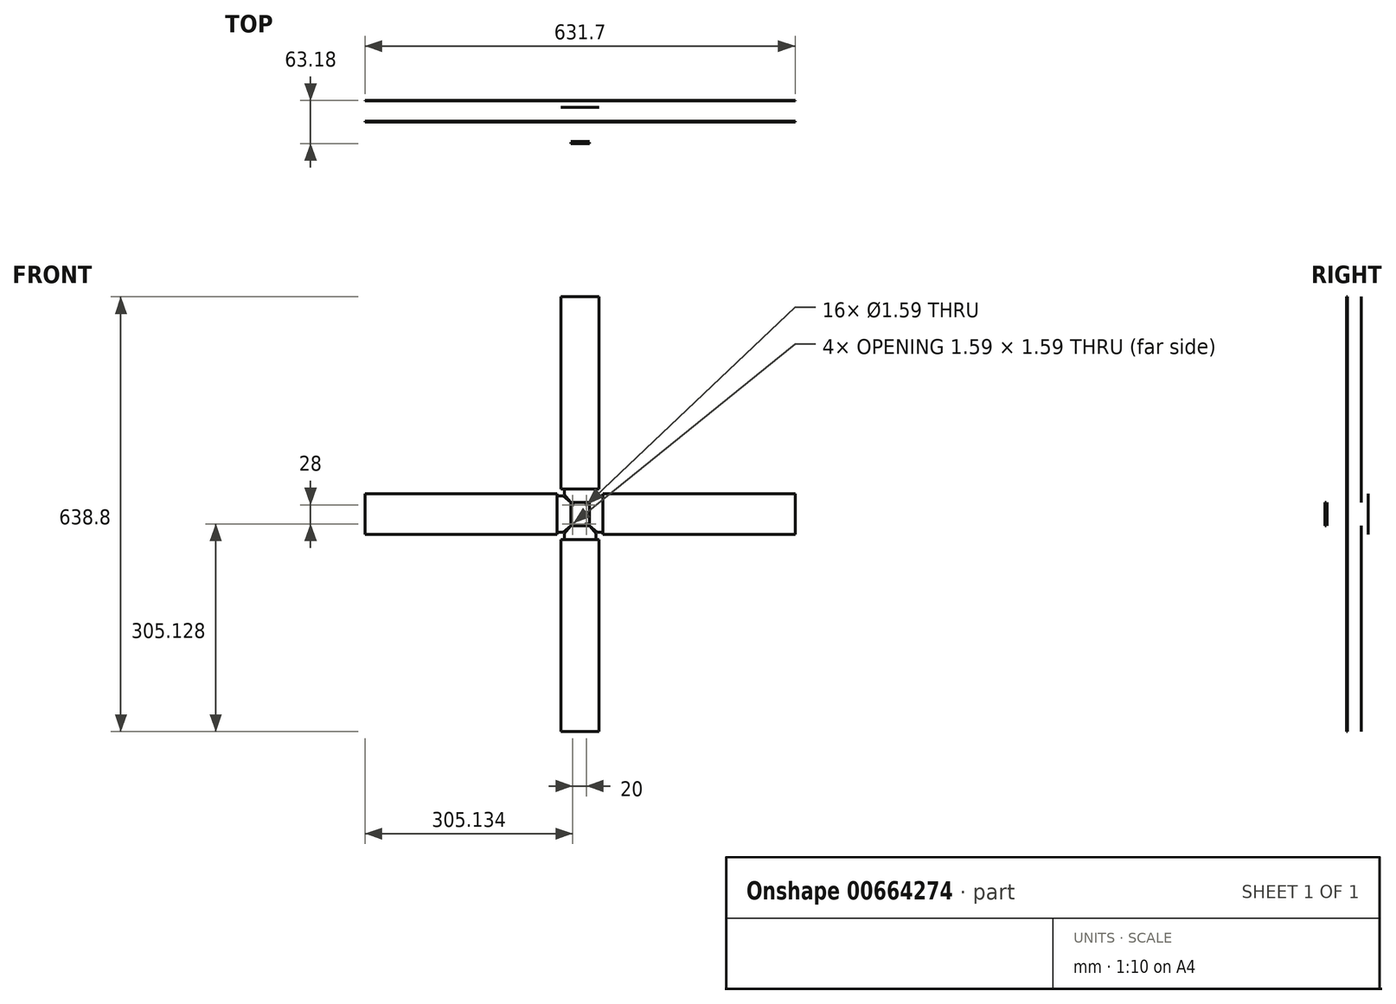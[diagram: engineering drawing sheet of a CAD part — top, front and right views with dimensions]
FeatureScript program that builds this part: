
annotation { "Feature Type Name" : "Feature", "Feature Type Description" : "" }
export const myFeature = defineFeature(function(context is Context, id is Id, definition is map)
    precondition{}
    {
        {
            var Q0;
            Q0=qCreatedBy(makeId("Front.planeOp"),FACE);
            var sketch = newSketch(context, id + "F0", { "sketchPlane" : qUnion([Q0])});
            skLineSegment(sketch, "E0.bottom", {"start": v(13.72, -17.27) * mm, "end": v(-13.72, -17.27) * mm});
            skLineSegment(sketch, "E0.top", {"start": v(13.72, 17.27) * mm, "end": v(-13.72, 17.27) * mm});
            skLineSegment(sketch, "E0.left", {"start": v(13.72, -17.27) * mm, "end": v(13.72, 17.27) * mm});
            skLineSegment(sketch, "E0.right", {"start": v(-13.72, -17.27) * mm, "end": v(-13.72, 17.27) * mm});
            skPoint(sketch, "E0.middle", {"position": v(0, 0) * mm});
            skLineSegment(sketch, "E1", {"start": v(0, 0) * mm, "end": v(200.92, 0) * mm, "construction": true});
            skLineSegment(sketch, "E2.bottom", {"start": v(33.66, -29.97) * mm, "end": v(315.85, -29.97) * mm});
            skLineSegment(sketch, "E2.top", {"start": v(33.66, 29.97) * mm, "end": v(315.85, 29.97) * mm});
            skLineSegment(sketch, "E2.left", {"start": v(33.66, -29.97) * mm, "end": v(33.66, 29.97) * mm});
            skLineSegment(sketch, "E2.right", {"start": v(315.85, -29.97) * mm, "end": v(315.85, 29.97) * mm});
            skLineSegment(sketch, "E3", {"start": v(33.66, 26.8) * mm, "end": v(25.07, 26.8) * mm});
            skLineSegment(sketch, "E4", {"start": v(25.07, 26.8) * mm, "end": v(13.72, 17.27) * mm});
            skLineSegment(sketch, "E5", {"start": v(33.66, -26.8) * mm, "end": v(25.07, -26.8) * mm});
            skLineSegment(sketch, "E6", {"start": v(25.07, -26.8) * mm, "end": v(13.72, -17.27) * mm});
            skLineSegment(sketch, "E7", {"start": v(0, 0) * mm, "end": v(0, 94.18) * mm, "construction": true});
            skLineSegment(sketch, "E8.bottom", {"start": v(-27.94, 37.21) * mm, "end": v(27.94, 37.21) * mm});
            skLineSegment(sketch, "E8.top", {"start": v(-27.94, 319.4) * mm, "end": v(27.94, 319.4) * mm});
            skLineSegment(sketch, "E8.left", {"start": v(-27.94, 37.21) * mm, "end": v(-27.94, 319.4) * mm});
            skLineSegment(sketch, "E8.right", {"start": v(27.94, 37.21) * mm, "end": v(27.94, 319.4) * mm});
            skLineSegment(sketch, "E9", {"start": v(-23.24, 37.21) * mm, "end": v(-23.24, 28.62) * mm});
            skLineSegment(sketch, "E10", {"start": v(-23.24, 28.62) * mm, "end": v(-13.72, 17.27) * mm});
            skLineSegment(sketch, "E11", {"start": v(23.24, 37.21) * mm, "end": v(23.24, 28.62) * mm});
            skLineSegment(sketch, "E12", {"start": v(23.24, 28.62) * mm, "end": v(13.72, 17.27) * mm});
            skSolve(sketch);
        }
        {
            var Q0;
            Q0=makeQuery(id+"F0.imprint","IMPRINT",FACE,{"disambiguationData":[TD([[makeQuery(id+"F0.imprint","IMPRINT",EDGE,{"derivedFrom":sQuery(id+"F0.wireOp",EDGE,"E0.bottom")}),-1.0]])]});
            extrude(context, id + "F1", {"entities" : qUnion([Q0]), "depth" : 0.2 * mm, "offsetDistance" : 25.4 * mm});
        }
        {
            var Q0;
            Q0=makeQuery(id+"F1.opExtrude","CAP_FACE",FACE,{"disambiguationData":[OSD([sQuery(id+"F0.wireOp",EDGE,"E0.bottom"),sQuery(id+"F0.wireOp",EDGE,"E0.top"),sQuery(id+"F0.wireOp",EDGE,"E0.right"),sQuery(id+"F0.wireOp",EDGE,"E2.bottom"),sQuery(id+"F0.wireOp",EDGE,"E2.top"),sQuery(id+"F0.wireOp",EDGE,"E2.left"),sQuery(id+"F0.wireOp",EDGE,"E2.right"),sQuery(id+"F0.wireOp",EDGE,"E3"),sQuery(id+"F0.wireOp",EDGE,"E4"),sQuery(id+"F0.wireOp",EDGE,"E5"),sQuery(id+"F0.wireOp",EDGE,"E6")])],"isStart":false});
            extrude(context, id + "F2", {"entities" : qUnion([Q0]), "depth" : (0.06 * 25.4 - 0.2) * mm, "offsetDistance" : 25 * mm});
        }
        {
            var Q0;
            Q0=makeQuery(id+"F0.imprint","IMPRINT",FACE,{"disambiguationData":[TD([[makeQuery(id+"F0.imprint","IMPRINT",EDGE,{"derivedFrom":sQuery(id+"F0.wireOp",EDGE,"E0.bottom")}),-1.0]])]});
            extrude(context, id + "F3", {"entities" : qUnion([Q0]), "depth" : (0.12 * 25.4) * mm, "offsetDistance" : 25 * mm});
        }
        {
            var Q0;
            Q0=makeQuery(id+"F2.opExtrude","SWEPT_BODY",BODY,{"disambiguationData":[OSD([sQuery(id+"F0.wireOp",EDGE,"E0.bottom"),sQuery(id+"F0.wireOp",EDGE,"E0.top"),sQuery(id+"F0.wireOp",EDGE,"E0.right"),sQuery(id+"F0.wireOp",EDGE,"E2.bottom"),sQuery(id+"F0.wireOp",EDGE,"E2.top"),sQuery(id+"F0.wireOp",EDGE,"E2.left"),sQuery(id+"F0.wireOp",EDGE,"E2.right"),sQuery(id+"F0.wireOp",EDGE,"E3"),sQuery(id+"F0.wireOp",EDGE,"E4"),sQuery(id+"F0.wireOp",EDGE,"E5"),sQuery(id+"F0.wireOp",EDGE,"E6")])]});
            var Q1;
            Q1=makeQuery(id+"F3.opExtrude","SWEPT_BODY",BODY,{"disambiguationData":[OSD([sQuery(id+"F0.wireOp",EDGE,"E0.bottom"),sQuery(id+"F0.wireOp",EDGE,"E0.top"),sQuery(id+"F0.wireOp",EDGE,"E0.left"),sQuery(id+"F0.wireOp",EDGE,"E0.right")])]});
            booleanBodies(context, id + "F4", {"operationType" : BooleanOperationType.SUBTRACTION, "tools" : qUnion([Q0]), "targets" : qUnion([Q1]), "keepTools" : true});
        }
        {
            var Q0;
            Q0=makeQuery(id+"F1.opExtrude","CAP_FACE",FACE,{"disambiguationData":[OSD([sQuery(id+"F0.wireOp",EDGE,"E0.bottom"),sQuery(id+"F0.wireOp",EDGE,"E0.top"),sQuery(id+"F0.wireOp",EDGE,"E0.right"),sQuery(id+"F0.wireOp",EDGE,"E2.bottom"),sQuery(id+"F0.wireOp",EDGE,"E2.top"),sQuery(id+"F0.wireOp",EDGE,"E2.left"),sQuery(id+"F0.wireOp",EDGE,"E2.right"),sQuery(id+"F0.wireOp",EDGE,"E3"),sQuery(id+"F0.wireOp",EDGE,"E4"),sQuery(id+"F0.wireOp",EDGE,"E5"),sQuery(id+"F0.wireOp",EDGE,"E6")])],"isStart":true});
            var sketch = newSketch(context, id + "F5", { "sketchPlane" : qUnion([Q0])});
            skCircle(sketch, "E13", {"center": v(10.72, -14.27) * mm, "radius": 0.8 * mm});
            skCircle(sketch, "E14.0.1.0", {"center": v(10.72, 13.73) * mm, "radius": 0.8 * mm});
            skCircle(sketch, "E14.1.0.0", {"center": v(-9.28, -14.27) * mm, "radius": 0.8 * mm});
            skCircle(sketch, "E14.1.1.0", {"center": v(-9.28, 13.73) * mm, "radius": 0.8 * mm});
            skLineSegment(sketch, "E14.direction1", {"start": v(-9.28, -14.27) * mm, "end": v(10.72, -14.27) * mm, "construction": true});
            skLineSegment(sketch, "E14.direction2", {"start": v(10.72, -14.27) * mm, "end": v(10.72, 13.73) * mm, "construction": true});
            skSolve(sketch);
        }
        {
            var Q0;
            Q0 = qSketchRegion(id + "F5", true);
            extrude(context, id + "F6", {"entities" : qUnion([Q0]), "operationType" : NewBodyOperationType.REMOVE, "endBound" : BoundingType.THROUGH_ALL, "oppositeDirection" : true, "depth" : 25 * mm, "offsetDistance" : 25 * mm});
        }
        {
            var Q0;
            Q0=makeQuery(id+"F0.imprint","IMPRINT",FACE,{"disambiguationData":[TD([[makeQuery(id+"F0.imprint","IMPRINT",EDGE,{"derivedFrom":sQuery(id+"F0.wireOp",EDGE,"E0.top")}),-1.0]])]});
            var Q1;
            Q1=makeQuery(id+"F0.imprint","IMPRINT",FACE,{"disambiguationData":[TD([[makeQuery(id+"F0.imprint","IMPRINT",EDGE,{"derivedFrom":sQuery(id+"F0.wireOp",EDGE,"E0.left")}),-1.0]])]});
            extrude(context, id + "F7", {"entities" : qUnion([Q0, Q1]), "depth" : 0.2 * mm, "offsetDistance" : 25 * mm});
        }
        {
            var Q0;
            Q0=makeQuery(id+"F0.imprint","IMPRINT",FACE,{"disambiguationData":[TD([[makeQuery(id+"F0.imprint","IMPRINT",EDGE,{"derivedFrom":sQuery(id+"F0.wireOp",EDGE,"E8.top")}),-1.0]])]});
            var Q1;
            {var subQ3=sQuery(id+"F0.wireOp",EDGE,"E2.bottom");Q1=makeQuery(id+"F0.imprint","IMPRINT",FACE,{"disambiguationData":[TD([[makeQuery(id+"F0.imprint","IMPRINT",EDGE,{"derivedFrom":subQ3}),1.0]])]});}
            extrude(context, id + "F8", {"entities" : qUnion([Q0, Q1]), "depth" : 0.2 * mm, "offsetDistance" : 25 * mm});
        }
        {
            var Q0;
            Q0=makeQuery(id+"F8.opExtrude","CAP_FACE",FACE,{"disambiguationData":[OSD([sQuery(id+"F0.wireOp",EDGE,"E8.bottom"),sQuery(id+"F0.wireOp",EDGE,"E8.top"),sQuery(id+"F0.wireOp",EDGE,"E8.left"),sQuery(id+"F0.wireOp",EDGE,"E8.right")])],"isStart":false});
            var Q1;
            Q1=makeQuery(id+"F8.opExtrude","CAP_FACE",FACE,{"disambiguationData":[OSD([sQuery(id+"F0.wireOp",EDGE,"E2.bottom"),sQuery(id+"F0.wireOp",EDGE,"E2.top"),sQuery(id+"F0.wireOp",EDGE,"E2.left"),sQuery(id+"F0.wireOp",EDGE,"E2.right")])],"isStart":false});
            var Q2;
            Q2=makeQuery(id+"F7.opExtrude","CAP_FACE",FACE,{"disambiguationData":[OSD([sQuery(id+"F0.wireOp",EDGE,"E0.top"),sQuery(id+"F0.wireOp",EDGE,"E8.bottom"),sQuery(id+"F0.wireOp",EDGE,"E9"),sQuery(id+"F0.wireOp",EDGE,"E10"),sQuery(id+"F0.wireOp",EDGE,"E11"),sQuery(id+"F0.wireOp",EDGE,"E12")])],"isStart":false});
            var Q3;
            Q3=makeQuery(id+"F7.opExtrude","CAP_FACE",FACE,{"disambiguationData":[OSD([sQuery(id+"F0.wireOp",EDGE,"E0.left"),sQuery(id+"F0.wireOp",EDGE,"E2.left"),sQuery(id+"F0.wireOp",EDGE,"E3"),sQuery(id+"F0.wireOp",EDGE,"E4"),sQuery(id+"F0.wireOp",EDGE,"E5"),sQuery(id+"F0.wireOp",EDGE,"E6")])],"isStart":false});
            extrude(context, id + "F9", {"entities" : qUnion([Q0, Q1, Q2, Q3]), "depth" : 1.3 * mm, "offsetDistance" : 25 * mm});
        }
        {
            var Q0;
            Q0=makeQuery(id+"F4.opBoolean","SPLIT",BODY,{"disambiguationData":[OD(1.0)],"derivedFrom":makeQuery(id+"F3.opExtrude","SWEPT_BODY",BODY,{"disambiguationData":[OSD([sQuery(id+"F0.wireOp",EDGE,"E0.bottom"),sQuery(id+"F0.wireOp",EDGE,"E0.top"),sQuery(id+"F0.wireOp",EDGE,"E0.left"),sQuery(id+"F0.wireOp",EDGE,"E0.right")])]})});
            transform(context, id + "F10", {"entities" : qUnion([Q0]), "transformType" : TransformType.TRANSLATION_3D, "dx" : 0 * mm, "dy" : -10 * mm, "dz" : 0 * mm, "makeCopy" : false});
        }
        {
            var Q0;
            Q0=makeQuery(id+"F1.opExtrude","SWEPT_BODY",BODY,{"disambiguationData":[OSD([sQuery(id+"F0.wireOp",EDGE,"E0.bottom"),sQuery(id+"F0.wireOp",EDGE,"E0.top"),sQuery(id+"F0.wireOp",EDGE,"E0.left"),sQuery(id+"F0.wireOp",EDGE,"E0.right")])]});
            var Q1;
            Q1=makeQuery(id+"F7.opExtrude","SWEPT_BODY",BODY,{"disambiguationData":[OSD([sQuery(id+"F0.wireOp",EDGE,"E0.left"),sQuery(id+"F0.wireOp",EDGE,"E2.left"),sQuery(id+"F0.wireOp",EDGE,"E3"),sQuery(id+"F0.wireOp",EDGE,"E4"),sQuery(id+"F0.wireOp",EDGE,"E5"),sQuery(id+"F0.wireOp",EDGE,"E6")])]});
            var Q2;
            Q2=makeQuery(id+"F8.opExtrude","SWEPT_BODY",BODY,{"disambiguationData":[OSD([sQuery(id+"F0.wireOp",EDGE,"E2.bottom"),sQuery(id+"F0.wireOp",EDGE,"E2.top"),sQuery(id+"F0.wireOp",EDGE,"E2.left"),sQuery(id+"F0.wireOp",EDGE,"E2.right")])]});
            transform(context, id + "F11", {"entities" : qUnion([Q0, Q1, Q2]), "transformType" : TransformType.TRANSLATION_3D, "dx" : 0 * mm, "dy" : 10 * mm, "dz" : 0 * mm, "makeCopy" : false});
        }
        {
            var Q0;
            Q0=makeQuery(id+"F8.opExtrude","SWEPT_BODY",BODY,{"disambiguationData":[OSD([sQuery(id+"F0.wireOp",EDGE,"E8.bottom"),sQuery(id+"F0.wireOp",EDGE,"E8.top"),sQuery(id+"F0.wireOp",EDGE,"E8.left"),sQuery(id+"F0.wireOp",EDGE,"E8.right")])]});
            var Q1;
            Q1=makeQuery(id+"F7.opExtrude","SWEPT_BODY",BODY,{"disambiguationData":[OSD([sQuery(id+"F0.wireOp",EDGE,"E0.top"),sQuery(id+"F0.wireOp",EDGE,"E8.bottom"),sQuery(id+"F0.wireOp",EDGE,"E9"),sQuery(id+"F0.wireOp",EDGE,"E10"),sQuery(id+"F0.wireOp",EDGE,"E11"),sQuery(id+"F0.wireOp",EDGE,"E12")])]});
            var Q2;
            Q2=makeQuery(id+"F9.opExtrude","SWEPT_BODY",BODY,{"disambiguationData":[OSD([sQuery(id+"F0.wireOp",EDGE,"E8.bottom"),sQuery(id+"F0.wireOp",EDGE,"E8.top"),sQuery(id+"F0.wireOp",EDGE,"E8.left"),sQuery(id+"F0.wireOp",EDGE,"E8.right")])]});
            var Q3;
            Q3=makeQuery(id+"F9.opExtrude","SWEPT_BODY",BODY,{"disambiguationData":[OSD([sQuery(id+"F0.wireOp",EDGE,"E0.top"),sQuery(id+"F0.wireOp",EDGE,"E8.bottom"),sQuery(id+"F0.wireOp",EDGE,"E9"),sQuery(id+"F0.wireOp",EDGE,"E10"),sQuery(id+"F0.wireOp",EDGE,"E11"),sQuery(id+"F0.wireOp",EDGE,"E12")])]});
            var Q4;
            Q4=qCreatedBy(makeId("Top.planeOp"),FACE);
            mirror(context, id + "F12", {"entities" : qUnion([Q0, Q1, Q2, Q3]), "mirrorPlane" : qUnion([Q4])});
        }
        {
            var Q0;
            Q0=makeQuery(id+"F8.opExtrude","SWEPT_BODY",BODY,{"disambiguationData":[OSD([sQuery(id+"F0.wireOp",EDGE,"E2.bottom"),sQuery(id+"F0.wireOp",EDGE,"E2.top"),sQuery(id+"F0.wireOp",EDGE,"E2.left"),sQuery(id+"F0.wireOp",EDGE,"E2.right")])]});
            var Q1;
            Q1=makeQuery(id+"F7.opExtrude","SWEPT_BODY",BODY,{"disambiguationData":[OSD([sQuery(id+"F0.wireOp",EDGE,"E0.left"),sQuery(id+"F0.wireOp",EDGE,"E2.left"),sQuery(id+"F0.wireOp",EDGE,"E3"),sQuery(id+"F0.wireOp",EDGE,"E4"),sQuery(id+"F0.wireOp",EDGE,"E5"),sQuery(id+"F0.wireOp",EDGE,"E6")])]});
            var Q2;
            Q2=makeQuery(id+"F9.opExtrude","SWEPT_BODY",BODY,{"disambiguationData":[OSD([sQuery(id+"F0.wireOp",EDGE,"E2.bottom"),sQuery(id+"F0.wireOp",EDGE,"E2.top"),sQuery(id+"F0.wireOp",EDGE,"E2.left"),sQuery(id+"F0.wireOp",EDGE,"E2.right")])]});
            var Q3;
            Q3=makeQuery(id+"F9.opExtrude","SWEPT_BODY",BODY,{"disambiguationData":[OSD([sQuery(id+"F0.wireOp",EDGE,"E0.left"),sQuery(id+"F0.wireOp",EDGE,"E2.left"),sQuery(id+"F0.wireOp",EDGE,"E3"),sQuery(id+"F0.wireOp",EDGE,"E4"),sQuery(id+"F0.wireOp",EDGE,"E5"),sQuery(id+"F0.wireOp",EDGE,"E6")])]});
            var Q4;
            Q4=qCreatedBy(makeId("Right.planeOp"),FACE);
            mirror(context, id + "F13", {"entities" : qUnion([Q0, Q1, Q2, Q3]), "mirrorPlane" : qUnion([Q4])});
        }
        {
            var Q0;
            Q0=makeQuery(id+"F4.opBoolean","SPLIT",BODY,{"disambiguationData":[OD(1.0)],"derivedFrom":makeQuery(id+"F3.opExtrude","SWEPT_BODY",BODY,{"disambiguationData":[OSD([sQuery(id+"F0.wireOp",EDGE,"E0.bottom"),sQuery(id+"F0.wireOp",EDGE,"E0.top"),sQuery(id+"F0.wireOp",EDGE,"E0.left"),sQuery(id+"F0.wireOp",EDGE,"E0.right")])]})});
            transform(context, id + "F14", {"entities" : qUnion([Q0]), "transformType" : TransformType.TRANSLATION_3D, "dx" : 0 * mm, "dy" : -20 * mm, "dz" : 0 * mm, "makeCopy" : false});
        }
        {
            var Q0;
            Q0=makeQuery(id+"F1.opExtrude","SWEPT_BODY",BODY,{"disambiguationData":[OSD([sQuery(id+"F0.wireOp",EDGE,"E0.bottom"),sQuery(id+"F0.wireOp",EDGE,"E0.top"),sQuery(id+"F0.wireOp",EDGE,"E0.right"),sQuery(id+"F0.wireOp",EDGE,"E2.bottom"),sQuery(id+"F0.wireOp",EDGE,"E2.top"),sQuery(id+"F0.wireOp",EDGE,"E2.left"),sQuery(id+"F0.wireOp",EDGE,"E2.right"),sQuery(id+"F0.wireOp",EDGE,"E3"),sQuery(id+"F0.wireOp",EDGE,"E4"),sQuery(id+"F0.wireOp",EDGE,"E5"),sQuery(id+"F0.wireOp",EDGE,"E6")])]});
            var Q1;
            Q1=makeQuery(id+"F13.opPattern","COPY",BODY,{"derivedFrom":makeQuery(id+"F7.opExtrude","SWEPT_BODY",BODY,{"disambiguationData":[OSD([sQuery(id+"F0.wireOp",EDGE,"E0.left"),sQuery(id+"F0.wireOp",EDGE,"E2.left"),sQuery(id+"F0.wireOp",EDGE,"E3"),sQuery(id+"F0.wireOp",EDGE,"E4"),sQuery(id+"F0.wireOp",EDGE,"E5"),sQuery(id+"F0.wireOp",EDGE,"E6")])]}),"instanceName":"1"});
            var Q2;
            Q2=makeQuery(id+"F7.opExtrude","SWEPT_BODY",BODY,{"disambiguationData":[OSD([sQuery(id+"F0.wireOp",EDGE,"E0.top"),sQuery(id+"F0.wireOp",EDGE,"E8.bottom"),sQuery(id+"F0.wireOp",EDGE,"E9"),sQuery(id+"F0.wireOp",EDGE,"E10"),sQuery(id+"F0.wireOp",EDGE,"E11"),sQuery(id+"F0.wireOp",EDGE,"E12")])]});
            var Q3;
            Q3=makeQuery(id+"F7.opExtrude","SWEPT_BODY",BODY,{"disambiguationData":[OSD([sQuery(id+"F0.wireOp",EDGE,"E0.left"),sQuery(id+"F0.wireOp",EDGE,"E2.left"),sQuery(id+"F0.wireOp",EDGE,"E3"),sQuery(id+"F0.wireOp",EDGE,"E4"),sQuery(id+"F0.wireOp",EDGE,"E5"),sQuery(id+"F0.wireOp",EDGE,"E6")])]});
            var Q4;
            Q4=makeQuery(id+"F12.opPattern","COPY",BODY,{"derivedFrom":makeQuery(id+"F7.opExtrude","SWEPT_BODY",BODY,{"disambiguationData":[OSD([sQuery(id+"F0.wireOp",EDGE,"E0.top"),sQuery(id+"F0.wireOp",EDGE,"E8.bottom"),sQuery(id+"F0.wireOp",EDGE,"E9"),sQuery(id+"F0.wireOp",EDGE,"E10"),sQuery(id+"F0.wireOp",EDGE,"E11"),sQuery(id+"F0.wireOp",EDGE,"E12")])]}),"instanceName":"1"});
            var Q5;
            Q5=makeQuery(id+"F12.opPattern","COPY",BODY,{"derivedFrom":makeQuery(id+"F8.opExtrude","SWEPT_BODY",BODY,{"disambiguationData":[OSD([sQuery(id+"F0.wireOp",EDGE,"E8.bottom"),sQuery(id+"F0.wireOp",EDGE,"E8.top"),sQuery(id+"F0.wireOp",EDGE,"E8.left"),sQuery(id+"F0.wireOp",EDGE,"E8.right")])]}),"instanceName":"1"});
            var Q6;
            Q6=makeQuery(id+"F8.opExtrude","SWEPT_BODY",BODY,{"disambiguationData":[OSD([sQuery(id+"F0.wireOp",EDGE,"E2.bottom"),sQuery(id+"F0.wireOp",EDGE,"E2.top"),sQuery(id+"F0.wireOp",EDGE,"E2.left"),sQuery(id+"F0.wireOp",EDGE,"E2.right")])]});
            var Q7;
            Q7=makeQuery(id+"F8.opExtrude","SWEPT_BODY",BODY,{"disambiguationData":[OSD([sQuery(id+"F0.wireOp",EDGE,"E8.bottom"),sQuery(id+"F0.wireOp",EDGE,"E8.top"),sQuery(id+"F0.wireOp",EDGE,"E8.left"),sQuery(id+"F0.wireOp",EDGE,"E8.right")])]});
            var Q8;
            Q8=makeQuery(id+"F13.opPattern","COPY",BODY,{"derivedFrom":makeQuery(id+"F8.opExtrude","SWEPT_BODY",BODY,{"disambiguationData":[OSD([sQuery(id+"F0.wireOp",EDGE,"E2.bottom"),sQuery(id+"F0.wireOp",EDGE,"E2.top"),sQuery(id+"F0.wireOp",EDGE,"E2.left"),sQuery(id+"F0.wireOp",EDGE,"E2.right")])]}),"instanceName":"1"});
            transform(context, id + "F15", {"entities" : qUnion([Q0, Q1, Q2, Q3, Q4, Q5, Q6, Q7, Q8]), "transformType" : TransformType.TRANSLATION_3D, "dx" : 0 * mm, "dy" : 20 * mm, "dz" : 0 * mm, "makeCopy" : false});
        }
    });
